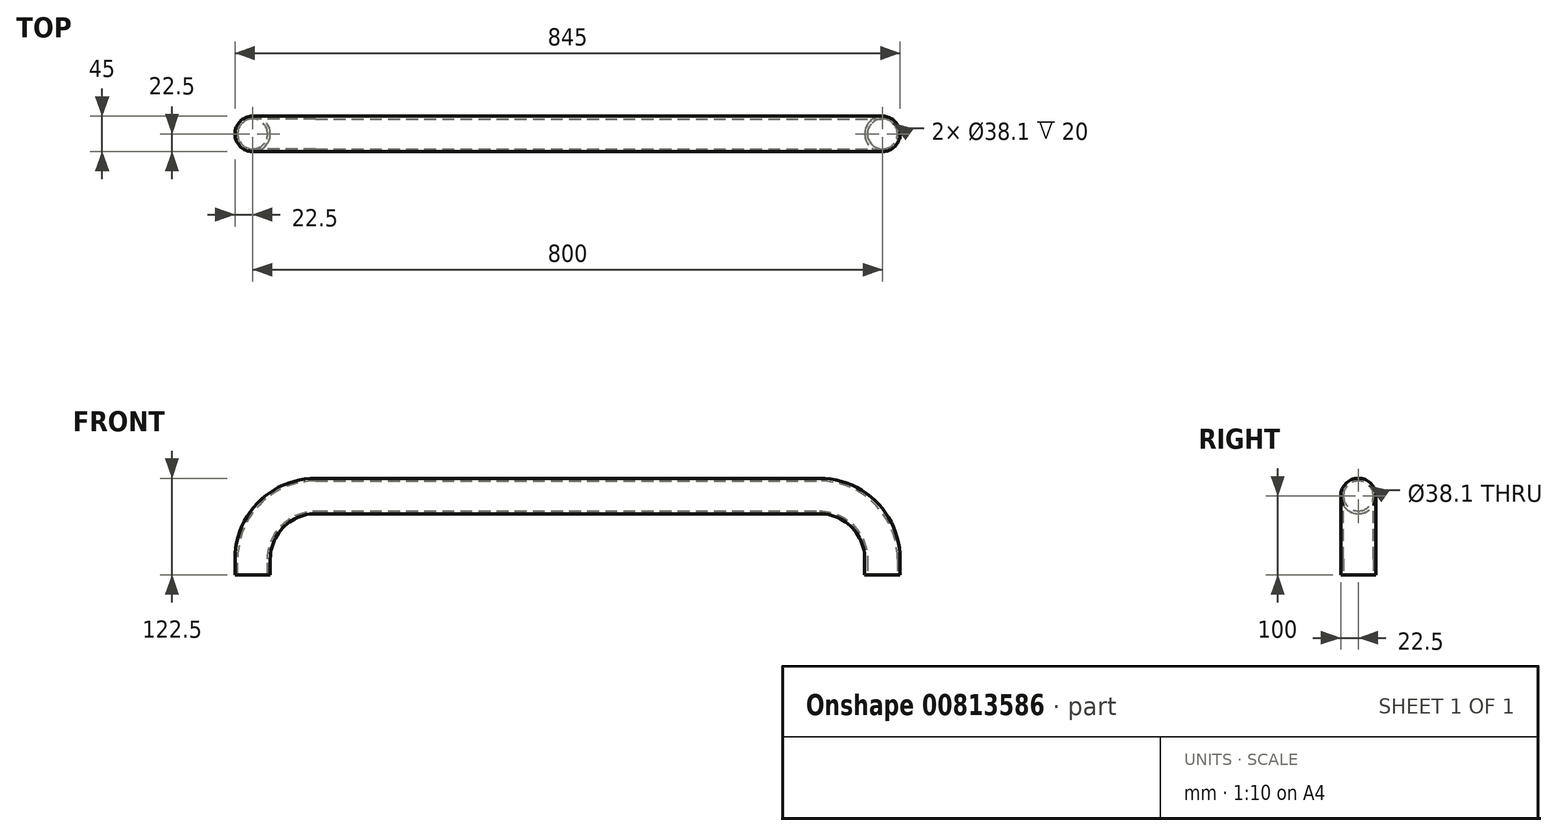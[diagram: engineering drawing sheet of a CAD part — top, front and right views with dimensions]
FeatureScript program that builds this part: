
annotation { "Feature Type Name" : "Feature", "Feature Type Description" : "" }
export const myFeature = defineFeature(function(context is Context, id is Id, definition is map)
    precondition{}
    {
        {
            var Q0;
            Q0=qCreatedBy(makeId("Top.planeOp"),FACE);
            var sketch = newSketch(context, id + "F0", { "sketchPlane" : qUnion([Q0])});
            skCircle(sketch, "E0", {"center": v(0, 0) * mm, "radius": 19.05 * mm});
            skCircle(sketch, "E1", {"center": v(0, 0) * mm, "radius": 22.5 * mm});
            skSolve(sketch);
        }
        {
            var Q0;
            Q0=qCreatedBy(makeId("Front.planeOp"),FACE);
            var sketch = newSketch(context, id + "F1", { "sketchPlane" : qUnion([Q0])});
            skLineSegment(sketch, "E2", {"start": v(0, 0) * mm, "end": v(0, 20) * mm});
            skLineSegment(sketch, "E3", {"start": v(80, 100) * mm, "end": v(720, 100) * mm});
            skLineSegment(sketch, "E4", {"start": v(800, 20) * mm, "end": v(800, 0) * mm});
            skPoint(sketch, "E5.visualSharp", {"position": v(0, 100) * mm});
            skArc(sketch, "E5.filletArc", {"start": v(80, 100) * mm, "mid": v(23.43, 76.57) * mm, "end": v(0, 20) * mm});
            skPoint(sketch, "E6.visualSharp", {"position": v(800, 100) * mm});
            skArc(sketch, "E6.filletArc", {"start": v(800, 20) * mm, "mid": v(776.57, 76.57) * mm, "end": v(720, 100) * mm});
            skSolve(sketch);
        }
        {
            var Q0;
            Q0=makeQuery(id+"F0.imprint","IMPRINT",FACE,{"disambiguationData":[TD([[makeQuery(id+"F0.imprint","IMPRINT",EDGE,{"derivedFrom":sQuery(id+"F0.wireOp",EDGE,"E0")}),-1.0]])]});
            var Q1;
            Q1=sQuery(id+"F1.wireOp",EDGE,"E2");
            var Q2;
            Q2=sQuery(id+"F1.wireOp",EDGE,"E5.filletArc");
            var Q3;
            Q3=sQuery(id+"F1.wireOp",EDGE,"E3");
            var Q4;
            Q4=sQuery(id+"F1.wireOp",EDGE,"E6.filletArc");
            var Q5;
            Q5=sQuery(id+"F1.wireOp",EDGE,"E4");
            sweep(context, id + "F2", {"profiles" : qUnion([Q0]), "path" : qUnion([Q1, Q2, Q3, Q4, Q5])});
        }
    });
